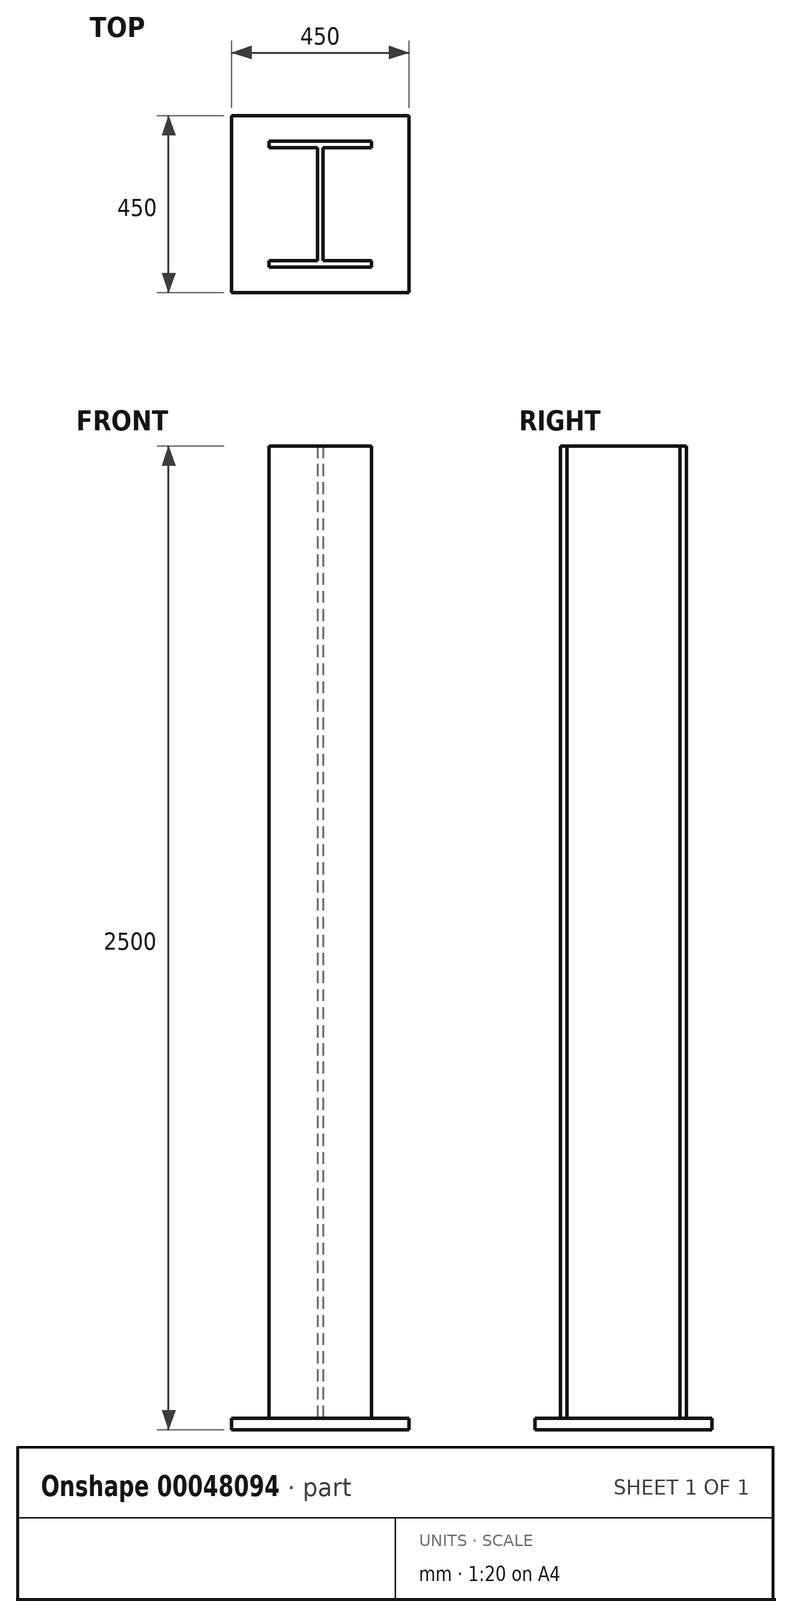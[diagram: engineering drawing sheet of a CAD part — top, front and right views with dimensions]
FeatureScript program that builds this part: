
annotation { "Feature Type Name" : "Feature", "Feature Type Description" : "" }
export const myFeature = defineFeature(function(context is Context, id is Id, definition is map)
    precondition{}
    {
        {
            var Q0;
            Q0=qCreatedBy(makeId("Top.planeOp"),FACE);
            var sketch = newSketch(context, id + "F0", { "sketchPlane" : qUnion([Q0])});
            skLineSegment(sketch, "E0.bottom", {"start": v(-1425, 225) * mm, "end": v(-975, 225) * mm});
            skLineSegment(sketch, "E0.top", {"start": v(-1425, -225) * mm, "end": v(-975, -225) * mm});
            skLineSegment(sketch, "E0.left", {"start": v(-1425, 225) * mm, "end": v(-1425, -225) * mm});
            skLineSegment(sketch, "E0.right", {"start": v(-975, 225) * mm, "end": v(-975, -225) * mm});
            skLineSegment(sketch, "E1", {"start": v(0, 0) * mm, "end": v(-2625, 0) * mm, "construction": true});
            skLineSegment(sketch, "E2", {"start": v(-2625, 0) * mm, "end": v(-2625, 582.23) * mm, "construction": true});
            skLineSegment(sketch, "E3", {"start": v(0, 0) * mm, "end": v(0, -617.01) * mm, "construction": true});
            skPoint(sketch, "E4", {"position": v(-1200, -225) * mm});
            skSolve(sketch);
        }
        {
            var Q0;
            Q0=makeQuery(id+"F0.imprint","IMPRINT",FACE,{"disambiguationData":[TD([[makeQuery(id+"F0.imprint","IMPRINT",EDGE,{"derivedFrom":sQuery(id+"F0.wireOp",EDGE,"E0.bottom")}),-1.0]])]});
            var sketch = newSketch(context, id + "F1", { "sketchPlane" : qUnion([Q0])});
            skLineSegment(sketch, "E5", {"start": v(-1330, 160) * mm, "end": v(-1070, 160) * mm});
            skLineSegment(sketch, "E6", {"start": v(-1070, 160) * mm, "end": v(-1070, 143.64) * mm});
            skLineSegment(sketch, "E7", {"start": v(-1070, 143.64) * mm, "end": v(-1192.5, 143.64) * mm});
            skLineSegment(sketch, "E8", {"start": v(-1192.5, 143.64) * mm, "end": v(-1192.5, -143.64) * mm});
            skLineSegment(sketch, "E9", {"start": v(-1192.5, -143.64) * mm, "end": v(-1070, -143.64) * mm});
            skLineSegment(sketch, "E10", {"start": v(-1070, -143.64) * mm, "end": v(-1070, -160) * mm});
            skLineSegment(sketch, "E11", {"start": v(-1070, -160) * mm, "end": v(-1330, -160) * mm});
            skLineSegment(sketch, "E12", {"start": v(-1330, -160) * mm, "end": v(-1330, -143.64) * mm});
            skLineSegment(sketch, "E13", {"start": v(-1330, -143.64) * mm, "end": v(-1207.5, -143.64) * mm});
            skLineSegment(sketch, "E14", {"start": v(-1207.5, -143.64) * mm, "end": v(-1207.5, 143.64) * mm});
            skLineSegment(sketch, "E15", {"start": v(-1207.5, 143.64) * mm, "end": v(-1330, 143.64) * mm});
            skLineSegment(sketch, "E16", {"start": v(-1330, 143.64) * mm, "end": v(-1330, 160) * mm});
            skLineSegment(sketch, "E17", {"start": v(-1200, -225) * mm, "end": v(-1200, 464.86) * mm, "construction": true});
            skPoint(sketch, "E18", {"position": v(-1200, 160) * mm});
            skPoint(sketch, "E19", {"position": v(-1192.5, 0) * mm});
            skLineSegment(sketch, "E20", {"start": v(-1425, 0) * mm, "end": v(-755.61, 0) * mm, "construction": true});
            skPoint(sketch, "E21", {"position": v(-1200, 0) * mm});
            skLineSegment(sketch, "E22", {"start": v(-1200, 1279.53) * mm, "end": v(-1200, 160) * mm, "construction": true});
            skSolve(sketch);
        }
        {
            var Q0;
            Q0=qSketchRegion(id+"F1",true);
            extrude(context, id + "F2", {"entities" : qUnion([Q0]), "depth" : 2470 * mm});
        }
        {
            var Q0;
            Q0=qSketchRegion(id+"F0",true);
            extrude(context, id + "F3", {"entities" : qUnion([Q0]), "operationType" : NewBodyOperationType.ADD, "oppositeDirection" : true, "depth" : 30 * mm});
        }
    });
